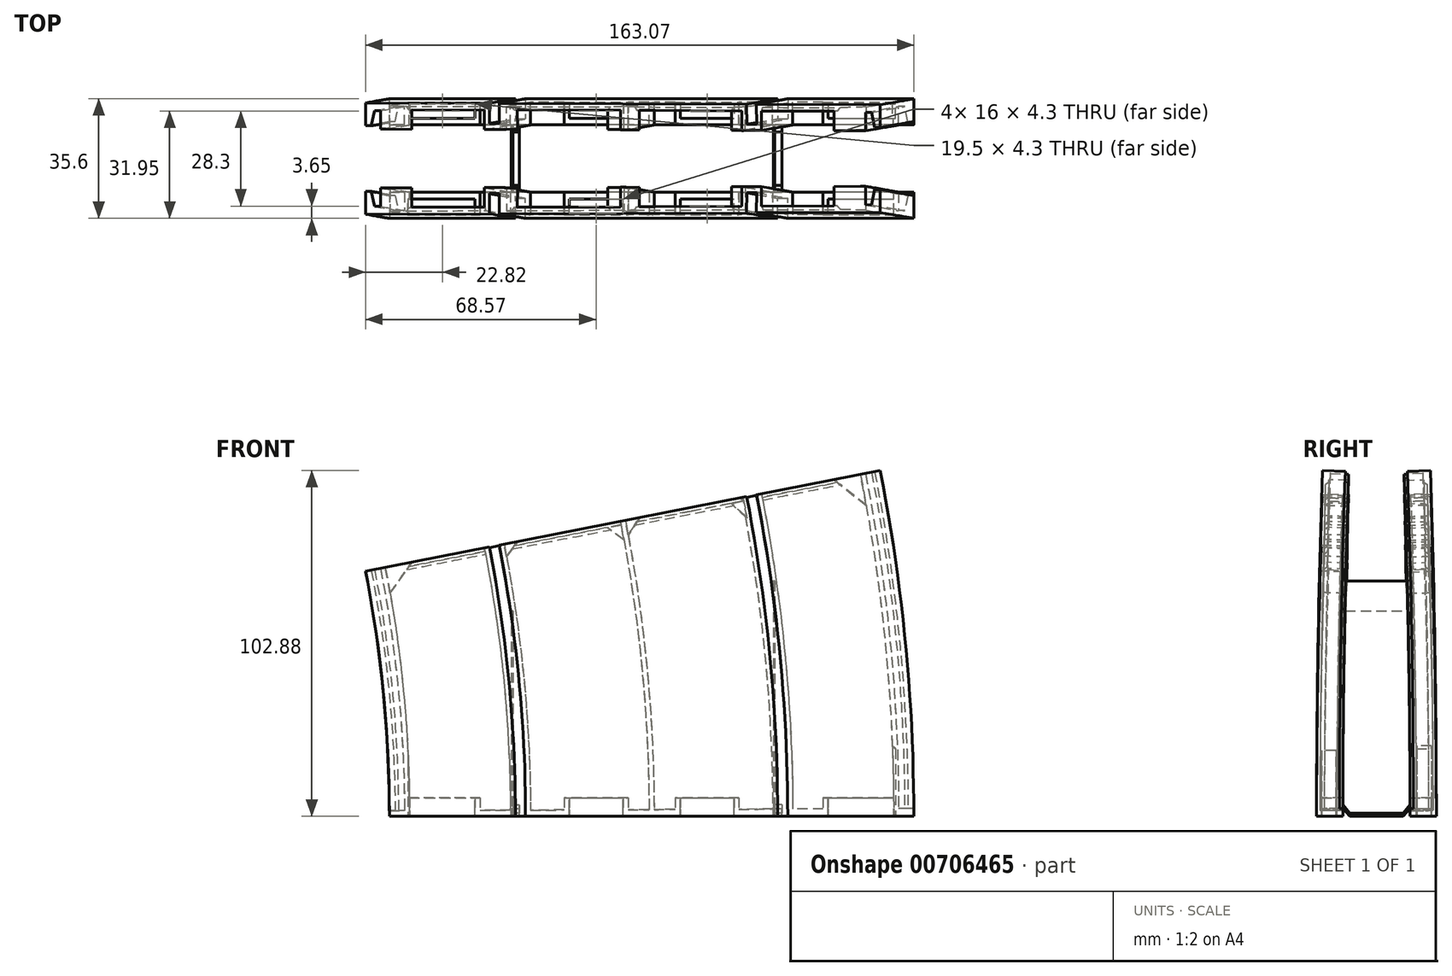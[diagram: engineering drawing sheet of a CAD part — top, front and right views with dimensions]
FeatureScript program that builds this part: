
annotation { "Feature Type Name" : "Feature", "Feature Type Description" : "" }
export const myFeature = defineFeature(function(context is Context, id is Id, definition is map)
    precondition{}
    {
        {
            var Q0;
            Q0=qCreatedBy(makeId("Top.planeOp"),FACE);
            var sketch = newSketch(context, id + "F0", { "sketchPlane" : qUnion([Q0])});
            skLineSegment(sketch, "E0", {"start": v(0, 7.8) * mm, "end": v(37.5, 7.8) * mm});
            skLineSegment(sketch, "E1", {"start": v(156, 0) * mm, "end": v(0, 0) * mm});
            skLineSegment(sketch, "E2", {"start": v(0, 0) * mm, "end": v(0, 7.8) * mm});
            skLineSegment(sketch, "E3.top", {"start": v(37.5, 1.8) * mm, "end": v(40.5, 1.8) * mm});
            skLineSegment(sketch, "E3.left", {"start": v(37.5, 7.8) * mm, "end": v(37.5, 1.8) * mm});
            skLineSegment(sketch, "E3.right", {"start": v(40.5, 7.8) * mm, "end": v(40.5, 1.8) * mm});
            skLineSegment(sketch, "E4.top", {"start": v(115.5, 1.8) * mm, "end": v(118.5, 1.8) * mm});
            skLineSegment(sketch, "E4.left", {"start": v(115.5, 7.8) * mm, "end": v(115.5, 1.8) * mm});
            skLineSegment(sketch, "E4.right", {"start": v(118.5, 7.8) * mm, "end": v(118.5, 1.8) * mm});
            skLineSegment(sketch, "E5.trimOffspring", {"start": v(40.5, 7.8) * mm, "end": v(115.5, 7.8) * mm});
            skLineSegment(sketch, "E6.trimOffspring", {"start": v(118.5, 7.8) * mm, "end": v(156, 7.8) * mm});
            skLineSegment(sketch, "E7.bottom", {"start": v(6, 6.3) * mm, "end": v(25.5, 6.3) * mm});
            skLineSegment(sketch, "E7.top", {"start": v(6, 2) * mm, "end": v(25.5, 2) * mm});
            skLineSegment(sketch, "E7.left", {"start": v(6, 6.3) * mm, "end": v(6, 2) * mm});
            skLineSegment(sketch, "E7.right", {"start": v(25.5, 6.3) * mm, "end": v(25.5, 2) * mm});
            skLineSegment(sketch, "E8.bottom", {"start": v(53.5, 6.3) * mm, "end": v(69.5, 6.3) * mm});
            skLineSegment(sketch, "E8.top", {"start": v(53.5, 2) * mm, "end": v(69.5, 2) * mm});
            skLineSegment(sketch, "E8.left", {"start": v(53.5, 6.3) * mm, "end": v(53.5, 2) * mm});
            skLineSegment(sketch, "E8.right", {"start": v(69.5, 6.3) * mm, "end": v(69.5, 2) * mm});
            skLineSegment(sketch, "E9.bottom", {"start": v(86.5, 6.3) * mm, "end": v(102.5, 6.3) * mm});
            skLineSegment(sketch, "E9.top", {"start": v(86.5, 2) * mm, "end": v(102.5, 2) * mm});
            skLineSegment(sketch, "E9.left", {"start": v(86.5, 6.3) * mm, "end": v(86.5, 2) * mm});
            skLineSegment(sketch, "E9.right", {"start": v(102.5, 6.3) * mm, "end": v(102.5, 2) * mm});
            skLineSegment(sketch, "E10.bottom", {"start": v(130.5, 6.3) * mm, "end": v(150, 6.3) * mm});
            skLineSegment(sketch, "E10.top", {"start": v(130.5, 2) * mm, "end": v(150, 2) * mm});
            skLineSegment(sketch, "E10.left", {"start": v(130.5, 6.3) * mm, "end": v(130.5, 2) * mm});
            skLineSegment(sketch, "E10.right", {"start": v(150, 6.3) * mm, "end": v(150, 2) * mm});
            skLineSegment(sketch, "E11", {"start": v(156, 7.8) * mm, "end": v(156, 0) * mm});
            skLineSegment(sketch, "E12", {"start": v(156, 0) * mm, "end": v(-362, -91.34) * mm});
            skLineSegment(sketch, "E13", {"start": v(-362, -91.34) * mm, "end": v(-356.5, -122.55) * mm});
            skSolve(sketch);
        }
        {
            var Q0;
            Q0=makeQuery(id+"F0.imprint","IMPRINT",FACE,{"disambiguationData":[TD([[makeQuery(id+"F0.imprint","IMPRINT",EDGE,{"derivedFrom":sQuery(id+"F0.wireOp",EDGE,"E0")}),-1.0]])]});
            var Q1;
            Q1=sQuery(id+"F0.wireOp",EDGE,"E13");
            revolve(context, id + "F1", {"surfaceOperationType" : NewSurfaceOperationType.NEW, "entities" : qUnion([Q0]), "axis" : qUnion([Q1]), "revolveType" : RevolveType.ONE_DIRECTION, "angle" : .25 * degree});
        }
        {
            var Q0;
            Q0=makeQuery(id+"F1.opRevolve","CAP_FACE",FACE,{"disambiguationData":[OSD([sQuery(id+"F0.wireOp",EDGE,"E0"),sQuery(id+"F0.wireOp",EDGE,"E1"),sQuery(id+"F0.wireOp",EDGE,"E2"),sQuery(id+"F0.wireOp",EDGE,"E3.top"),sQuery(id+"F0.wireOp",EDGE,"E3.left"),sQuery(id+"F0.wireOp",EDGE,"E3.right"),sQuery(id+"F0.wireOp",EDGE,"E4.top"),sQuery(id+"F0.wireOp",EDGE,"E4.left"),sQuery(id+"F0.wireOp",EDGE,"E4.right"),sQuery(id+"F0.wireOp",EDGE,"E5.trimOffspring"),sQuery(id+"F0.wireOp",EDGE,"E6.trimOffspring"),sQuery(id+"F0.wireOp",EDGE,"E7.bottom"),sQuery(id+"F0.wireOp",EDGE,"E7.top"),sQuery(id+"F0.wireOp",EDGE,"E7.left"),sQuery(id+"F0.wireOp",EDGE,"E7.right"),sQuery(id+"F0.wireOp",EDGE,"E8.bottom"),sQuery(id+"F0.wireOp",EDGE,"E8.top"),sQuery(id+"F0.wireOp",EDGE,"E8.left"),sQuery(id+"F0.wireOp",EDGE,"E8.right"),sQuery(id+"F0.wireOp",EDGE,"E9.bottom"),sQuery(id+"F0.wireOp",EDGE,"E9.top"),sQuery(id+"F0.wireOp",EDGE,"E9.left"),sQuery(id+"F0.wireOp",EDGE,"E9.right"),sQuery(id+"F0.wireOp",EDGE,"E10.bottom"),sQuery(id+"F0.wireOp",EDGE,"E10.top"),sQuery(id+"F0.wireOp",EDGE,"E10.left"),sQuery(id+"F0.wireOp",EDGE,"E10.right"),sQuery(id+"F0.wireOp",EDGE,"E11")])],"isStart":true});
            var sketch = newSketch(context, id + "F2", { "sketchPlane" : qUnion([Q0])});
            skLineSegment(sketch, "E14", {"start": v(156, -1) * mm, "end": v(154.3, -1) * mm});
            skLineSegment(sketch, "E15", {"start": v(154.3, -1) * mm, "end": v(153.3, -5.5) * mm});
            skLineSegment(sketch, "E16", {"start": v(153.3, -5.5) * mm, "end": v(151.5, -5.5) * mm});
            skLineSegment(sketch, "E17", {"start": v(151.5, -5.5) * mm, "end": v(151.5, 0) * mm});
            skLineSegment(sketch, "E18", {"start": v(151.5, 0) * mm, "end": v(150, 0) * mm});
            skLineSegment(sketch, "E19", {"start": v(150, 0) * mm, "end": v(150, -6.8) * mm});
            skLineSegment(sketch, "E20", {"start": v(150, -6.8) * mm, "end": v(120, -6.8) * mm});
            skLineSegment(sketch, "E21", {"start": v(120, -6.8) * mm, "end": v(120, 0) * mm});
            skLineSegment(sketch, "E22", {"start": v(120, 0) * mm, "end": v(114, 0) * mm});
            skLineSegment(sketch, "E23", {"start": v(114, 0) * mm, "end": v(114, -6.8) * mm});
            skLineSegment(sketch, "E24", {"start": v(114, -6.8) * mm, "end": v(78.75, -6.8) * mm});
            skLineSegment(sketch, "E25", {"start": v(42, -6.8) * mm, "end": v(42, 0) * mm});
            skLineSegment(sketch, "E26", {"start": v(42, 0) * mm, "end": v(36, 0) * mm});
            skLineSegment(sketch, "E27", {"start": v(36, 0) * mm, "end": v(36, -6.8) * mm});
            skLineSegment(sketch, "E28", {"start": v(36, -6.8) * mm, "end": v(6, -6.8) * mm});
            skLineSegment(sketch, "E29", {"start": v(6, -6.8) * mm, "end": v(6, 0) * mm});
            skLineSegment(sketch, "E30", {"start": v(6, 0) * mm, "end": v(4.5, 0) * mm});
            skLineSegment(sketch, "E31", {"start": v(4.5, 0) * mm, "end": v(4.5, -5.5) * mm});
            skLineSegment(sketch, "E32", {"start": v(4.5, -5.5) * mm, "end": v(2.7, -5.5) * mm});
            skLineSegment(sketch, "E33", {"start": v(2.7, -5.5) * mm, "end": v(1.7, -1) * mm});
            skLineSegment(sketch, "E34", {"start": v(1.7, -1) * mm, "end": v(0, -1) * mm});
            skLineSegment(sketch, "E35", {"start": v(0, -1) * mm, "end": v(0, -7.8) * mm});
            skLineSegment(sketch, "E36", {"start": v(0, -7.8) * mm, "end": v(156, -7.8) * mm});
            skLineSegment(sketch, "E37", {"start": v(156, -7.8) * mm, "end": v(156, -1) * mm});
            skLineSegment(sketch, "E38", {"start": v(77.25, 0) * mm, "end": v(77.25, -6.8) * mm});
            skLineSegment(sketch, "E39.trimOffspring", {"start": v(77.25, -6.8) * mm, "end": v(42, -6.8) * mm});
            skLineSegment(sketch, "E40", {"start": v(156, 0) * mm, "end": v(-362, 91.34) * mm});
            skLineSegment(sketch, "E41", {"start": v(-362, 91.34) * mm, "end": v(-367.9, 57.9) * mm});
            skLineSegment(sketch, "E42", {"start": v(78.75, 0) * mm, "end": v(78.75, -6.8) * mm});
            skLineSegment(sketch, "E43", {"start": v(77.25, 0) * mm, "end": v(78.75, 0) * mm});
            skSolve(sketch);
        }
        {
            var Q0;
            Q0=makeQuery(id+"F2.imprint","IMPRINT",FACE,{"disambiguationData":[TD([[makeQuery(id+"F2.imprint","IMPRINT",EDGE,{"derivedFrom":sQuery(id+"F2.wireOp",EDGE,"E14")}),1.0]])]});
            var Q1;
            Q1=sQuery(id+"F2.wireOp",EDGE,"E41");
            revolve(context, id + "F3", {"operationType" : NewBodyOperationType.ADD, "surfaceOperationType" : NewSurfaceOperationType.NEW, "entities" : qUnion([Q0]), "axis" : qUnion([Q1]), "revolveType" : RevolveType.ONE_DIRECTION, "oppositeDirection" : true, "angle" : 11.25 * degree});
        }
        {
            var Q0;
            Q0=makeQuery(id+"F1.opRevolve","CAP_FACE",FACE,{"disambiguationData":[OSD([sQuery(id+"F0.wireOp",EDGE,"E0"),sQuery(id+"F0.wireOp",EDGE,"E1"),sQuery(id+"F0.wireOp",EDGE,"E2"),sQuery(id+"F0.wireOp",EDGE,"E3.top"),sQuery(id+"F0.wireOp",EDGE,"E3.left"),sQuery(id+"F0.wireOp",EDGE,"E3.right"),sQuery(id+"F0.wireOp",EDGE,"E4.top"),sQuery(id+"F0.wireOp",EDGE,"E4.left"),sQuery(id+"F0.wireOp",EDGE,"E4.right"),sQuery(id+"F0.wireOp",EDGE,"E5.trimOffspring"),sQuery(id+"F0.wireOp",EDGE,"E6.trimOffspring"),sQuery(id+"F0.wireOp",EDGE,"E7.bottom"),sQuery(id+"F0.wireOp",EDGE,"E7.top"),sQuery(id+"F0.wireOp",EDGE,"E7.left"),sQuery(id+"F0.wireOp",EDGE,"E7.right"),sQuery(id+"F0.wireOp",EDGE,"E8.bottom"),sQuery(id+"F0.wireOp",EDGE,"E8.top"),sQuery(id+"F0.wireOp",EDGE,"E8.left"),sQuery(id+"F0.wireOp",EDGE,"E8.right"),sQuery(id+"F0.wireOp",EDGE,"E9.bottom"),sQuery(id+"F0.wireOp",EDGE,"E9.top"),sQuery(id+"F0.wireOp",EDGE,"E9.left"),sQuery(id+"F0.wireOp",EDGE,"E9.right"),sQuery(id+"F0.wireOp",EDGE,"E10.bottom"),sQuery(id+"F0.wireOp",EDGE,"E10.top"),sQuery(id+"F0.wireOp",EDGE,"E10.left"),sQuery(id+"F0.wireOp",EDGE,"E10.right"),sQuery(id+"F0.wireOp",EDGE,"E11")])],"isStart":true});
            var sketch = newSketch(context, id + "F4", { "sketchPlane" : qUnion([Q0])});
            skLineSegment(sketch, "E44.bottom", {"start": v(6, -2) * mm, "end": v(25.5, -2) * mm});
            skLineSegment(sketch, "E44.top", {"start": v(6, -6.3) * mm, "end": v(25.5, -6.3) * mm});
            skLineSegment(sketch, "E44.left", {"start": v(6, -2) * mm, "end": v(6, -6.3) * mm});
            skLineSegment(sketch, "E44.right", {"start": v(25.5, -2) * mm, "end": v(25.5, -6.3) * mm});
            skLineSegment(sketch, "E45.bottom", {"start": v(53.5, -2) * mm, "end": v(69.5, -2) * mm});
            skLineSegment(sketch, "E45.top", {"start": v(53.5, -6.3) * mm, "end": v(69.5, -6.3) * mm});
            skLineSegment(sketch, "E45.left", {"start": v(53.5, -2) * mm, "end": v(53.5, -6.3) * mm});
            skLineSegment(sketch, "E45.right", {"start": v(69.5, -2) * mm, "end": v(69.5, -6.3) * mm});
            skLineSegment(sketch, "E46.bottom", {"start": v(86.5, -2) * mm, "end": v(102.5, -2) * mm});
            skLineSegment(sketch, "E46.top", {"start": v(86.5, -6.3) * mm, "end": v(102.5, -6.3) * mm});
            skLineSegment(sketch, "E46.left", {"start": v(86.5, -2) * mm, "end": v(86.5, -6.3) * mm});
            skLineSegment(sketch, "E46.right", {"start": v(102.5, -2) * mm, "end": v(102.5, -6.3) * mm});
            skLineSegment(sketch, "E47.bottom", {"start": v(130.5, -2) * mm, "end": v(150, -2) * mm});
            skLineSegment(sketch, "E47.top", {"start": v(130.5, -6.3) * mm, "end": v(150, -6.3) * mm});
            skLineSegment(sketch, "E47.left", {"start": v(130.5, -2) * mm, "end": v(130.5, -6.3) * mm});
            skLineSegment(sketch, "E47.right", {"start": v(150, -2) * mm, "end": v(150, -6.3) * mm});
            skLineSegment(sketch, "E48.bottom", {"start": v(4.5, 0) * mm, "end": v(27, 0) * mm});
            skLineSegment(sketch, "E48.top", {"start": v(4.5, -7.8) * mm, "end": v(27, -7.8) * mm});
            skLineSegment(sketch, "E48.left", {"start": v(4.5, 0) * mm, "end": v(4.5, -7.8) * mm});
            skLineSegment(sketch, "E48.right", {"start": v(27, 0) * mm, "end": v(27, -7.8) * mm});
            skLineSegment(sketch, "E49.bottom", {"start": v(52, 0) * mm, "end": v(71, 0) * mm});
            skLineSegment(sketch, "E49.top", {"start": v(52, -7.8) * mm, "end": v(71, -7.8) * mm});
            skLineSegment(sketch, "E49.left", {"start": v(52, 0) * mm, "end": v(52, -7.8) * mm});
            skLineSegment(sketch, "E49.right", {"start": v(71, 0) * mm, "end": v(71, -7.8) * mm});
            skLineSegment(sketch, "E50.bottom", {"start": v(85, 0) * mm, "end": v(104, 0) * mm});
            skLineSegment(sketch, "E50.top", {"start": v(85, -7.8) * mm, "end": v(104, -7.8) * mm});
            skLineSegment(sketch, "E50.left", {"start": v(85, 0) * mm, "end": v(85, -7.8) * mm});
            skLineSegment(sketch, "E50.right", {"start": v(104, 0) * mm, "end": v(104, -7.8) * mm});
            skLineSegment(sketch, "E51.bottom", {"start": v(129, 0) * mm, "end": v(151.4, 0) * mm});
            skLineSegment(sketch, "E51.top", {"start": v(129, -7.8) * mm, "end": v(151.4, -7.8) * mm});
            skLineSegment(sketch, "E51.left", {"start": v(129, 0) * mm, "end": v(129, -7.8) * mm});
            skLineSegment(sketch, "E51.right", {"start": v(151.4, 0) * mm, "end": v(151.4, -7.8) * mm});
            skSolve(sketch);
        }
        {
            var Q0;
            Q0=makeQuery(id+"F4.imprint","IMPRINT",FACE,{"disambiguationData":[TD([[makeQuery(id+"F4.imprint","IMPRINT",EDGE,{"derivedFrom":sQuery(id+"F4.wireOp",EDGE,"E44.bottom")}),1.0]])]});
            var Q1;
            Q1=makeQuery(id+"F4.imprint","IMPRINT",FACE,{"disambiguationData":[TD([[makeQuery(id+"F4.imprint","IMPRINT",EDGE,{"derivedFrom":sQuery(id+"F4.wireOp",EDGE,"E45.bottom")}),1.0]])]});
            var Q2;
            Q2=makeQuery(id+"F4.imprint","IMPRINT",FACE,{"disambiguationData":[TD([[makeQuery(id+"F4.imprint","IMPRINT",EDGE,{"derivedFrom":sQuery(id+"F4.wireOp",EDGE,"E46.bottom")}),1.0]])]});
            var Q3;
            Q3=makeQuery(id+"F4.imprint","IMPRINT",FACE,{"disambiguationData":[TD([[makeQuery(id+"F4.imprint","IMPRINT",EDGE,{"derivedFrom":sQuery(id+"F4.wireOp",EDGE,"E47.bottom")}),1.0]])]});
            extrude(context, id + "F5", {"entities" : qUnion([Q0, Q1, Q2, Q3]), "operationType" : NewBodyOperationType.ADD, "oppositeDirection" : true, "depth" : 5.5 * mm, "offsetDistance" : 25 * mm});
        }
        {
            var Q0;
            Q0=makeQuery(id+"F3.opRevolve","CAP_FACE",FACE,{"disambiguationData":[OSD([sQuery(id+"F0.wireOp",EDGE,"E3.top"),sQuery(id+"F0.wireOp",EDGE,"E3.left"),sQuery(id+"F0.wireOp",EDGE,"E3.right"),sQuery(id+"F0.wireOp",EDGE,"E4.top"),sQuery(id+"F0.wireOp",EDGE,"E4.left"),sQuery(id+"F0.wireOp",EDGE,"E4.right"),sQuery(id+"F2.wireOp",EDGE,"E14"),sQuery(id+"F2.wireOp",EDGE,"E15"),sQuery(id+"F2.wireOp",EDGE,"E16"),sQuery(id+"F2.wireOp",EDGE,"E17"),sQuery(id+"F2.wireOp",EDGE,"E18"),sQuery(id+"F2.wireOp",EDGE,"E19"),sQuery(id+"F2.wireOp",EDGE,"E20"),sQuery(id+"F2.wireOp",EDGE,"E21"),sQuery(id+"F2.wireOp",EDGE,"E22"),sQuery(id+"F2.wireOp",EDGE,"E23"),sQuery(id+"F2.wireOp",EDGE,"E24"),sQuery(id+"F2.wireOp",EDGE,"E25"),sQuery(id+"F2.wireOp",EDGE,"E26"),sQuery(id+"F2.wireOp",EDGE,"E27"),sQuery(id+"F2.wireOp",EDGE,"E28"),sQuery(id+"F2.wireOp",EDGE,"E29"),sQuery(id+"F2.wireOp",EDGE,"E30"),sQuery(id+"F2.wireOp",EDGE,"E31"),sQuery(id+"F2.wireOp",EDGE,"E32"),sQuery(id+"F2.wireOp",EDGE,"E33"),sQuery(id+"F2.wireOp",EDGE,"E34"),sQuery(id+"F2.wireOp",EDGE,"E35"),sQuery(id+"F2.wireOp",EDGE,"E36"),sQuery(id+"F2.wireOp",EDGE,"E37"),sQuery(id+"F2.wireOp",EDGE,"E38"),sQuery(id+"F2.wireOp",EDGE,"E39.trimOffspring"),sQuery(id+"F2.wireOp",EDGE,"E42"),sQuery(id+"F2.wireOp",EDGE,"E43")])],"isStart":false});
            var sketch = newSketch(context, id + "F6", { "sketchPlane" : qUnion([Q0])});
            skLineSegment(sketch, "E52", {"start": v(12.1, 8.09) * mm, "end": v(43.02, 8.19) * mm});
            skLineSegment(sketch, "E53", {"start": v(43.02, 8.19) * mm, "end": v(43.02, 7.2) * mm});
            skLineSegment(sketch, "E54", {"start": v(43.02, 7.2) * mm, "end": v(12.07, 7.09) * mm});
            skLineSegment(sketch, "E55", {"start": v(12.07, 7.09) * mm, "end": v(12.1, 8.09) * mm});
            skLineSegment(sketch, "E56", {"start": v(84.27, 8.32) * mm, "end": v(84.27, 7.44) * mm});
            skLineSegment(sketch, "E57", {"start": v(84.27, 7.44) * mm, "end": v(48.45, 7.32) * mm});
            skLineSegment(sketch, "E58", {"start": v(48.45, 7.32) * mm, "end": v(48.45, 8.32) * mm});
            skLineSegment(sketch, "E59", {"start": v(48.45, 8.32) * mm, "end": v(84.27, 8.32) * mm});
            skLineSegment(sketch, "E60", {"start": v(121.02, 8.45) * mm, "end": v(121.02, 7.45) * mm});
            skLineSegment(sketch, "E61", {"start": v(121.02, 7.45) * mm, "end": v(85.29, 7.45) * mm});
            skLineSegment(sketch, "E62", {"start": v(85.29, 7.45) * mm, "end": v(85.29, 8.45) * mm});
            skLineSegment(sketch, "E63", {"start": v(85.29, 8.45) * mm, "end": v(121.02, 8.45) * mm});
            skLineSegment(sketch, "E64", {"start": v(163.93, 8.6) * mm, "end": v(163.93, 7.6) * mm});
            skLineSegment(sketch, "E65", {"start": v(163.93, 7.6) * mm, "end": v(126.5, 7.47) * mm});
            skLineSegment(sketch, "E66", {"start": v(126.5, 7.47) * mm, "end": v(126.5, 8.47) * mm});
            skLineSegment(sketch, "E67", {"start": v(126.5, 8.47) * mm, "end": v(163.93, 8.6) * mm});
            skSolve(sketch);
        }
        {
            var Q0;
            {var subQ0=sQuery(id+"F6.wireOp",EDGE,"E53");Q0=makeQuery(id+"F6.imprint","IMPRINT",FACE,{"disambiguationData":[TD([[makeQuery(id+"F6.imprint","IMPRINT",EDGE,{"derivedFrom":subQ0}),1.0]])]});}
            var Q1;
            Q1=makeQuery(id+"F6.imprint","IMPRINT",FACE,{"disambiguationData":[TD([[makeQuery(id+"F6.imprint","IMPRINT",EDGE,{"derivedFrom":sQuery(id+"F6.wireOp",EDGE,"E52")}),-1.0]])]});
            var Q2;
            {var subQ0=sQuery(id+"F6.wireOp",EDGE,"E56");Q2=makeQuery(id+"F6.imprint","IMPRINT",FACE,{"disambiguationData":[TD([[makeQuery(id+"F6.imprint","IMPRINT",EDGE,{"derivedFrom":subQ0}),1.0]])]});}
            var Q3;
            {var subQ1=sQuery(id+"F6.wireOp",EDGE,"E58");Q3=makeQuery(id+"F6.imprint","IMPRINT",FACE,{"disambiguationData":[TD([[makeQuery(id+"F6.imprint","IMPRINT",EDGE,{"derivedFrom":subQ1}),-1.0]])]});}
            var Q4;
            {var subQ0=sQuery(id+"F6.wireOp",EDGE,"E60");Q4=makeQuery(id+"F6.imprint","IMPRINT",FACE,{"disambiguationData":[TD([[makeQuery(id+"F6.imprint","IMPRINT",EDGE,{"derivedFrom":subQ0}),1.0]])]});}
            var Q5;
            {var subQ0=sQuery(id+"F6.wireOp",EDGE,"E62");Q5=makeQuery(id+"F6.imprint","IMPRINT",FACE,{"disambiguationData":[TD([[makeQuery(id+"F6.imprint","IMPRINT",EDGE,{"derivedFrom":subQ0}),-1.0]])]});}
            var Q6;
            {var subQ0=sQuery(id+"F6.wireOp",EDGE,"E65");var subQ1=makeQuery(id+"F3.opRevolve","CAP_EDGE",EDGE,{"disambiguationData":[OSD([sQuery(id+"F2.wireOp",EDGE,"E19")])],"isStart":false});var subQ2=makeQuery(id+"F6.imprint","INTERSECT",VERTEX,{"derivedFrom":[subQ1,subQ0]});Q6=makeQuery(id+"F6.imprint","IMPRINT",FACE,{"disambiguationData":[TD([[makeQuery(id+"F6.imprint","IMPRINT",EDGE,{"disambiguationData":[TD([[subQ2,-1.0]])],"derivedFrom":subQ0}),-1.0]])]});}
            var Q7;
            {var subQ0=sQuery(id+"F6.wireOp",EDGE,"E66");Q7=makeQuery(id+"F6.imprint","IMPRINT",FACE,{"disambiguationData":[TD([[makeQuery(id+"F6.imprint","IMPRINT",EDGE,{"derivedFrom":subQ0}),-1.0]])]});}
            var Q8;
            {var subQ0=sQuery(id+"F6.wireOp",EDGE,"E65");var subQ1=makeQuery(id+"F3.opRevolve","CAP_EDGE",EDGE,{"disambiguationData":[OSD([sQuery(id+"F2.wireOp",EDGE,"E37")])],"isStart":false});var subQ2=makeQuery(id+"F6.imprint","INTERSECT",VERTEX,{"derivedFrom":[subQ1,subQ0]});Q8=makeQuery(id+"F6.imprint","IMPRINT",FACE,{"disambiguationData":[TD([[makeQuery(id+"F6.imprint","IMPRINT",EDGE,{"disambiguationData":[TD([[subQ2,-1.0]])],"derivedFrom":subQ0}),-1.0]])]});}
            var Q9;
            {var subQ0=sQuery(id+"F6.wireOp",EDGE,"E64");Q9=makeQuery(id+"F6.imprint","IMPRINT",FACE,{"disambiguationData":[TD([[makeQuery(id+"F6.imprint","IMPRINT",EDGE,{"derivedFrom":subQ0}),-1.0]])]});}
            extrude(context, id + "F7", {"entities" : qUnion([Q0, Q1, Q2, Q3, Q4, Q5, Q6, Q7, Q8, Q9]), "operationType" : NewBodyOperationType.ADD, "oppositeDirection" : true, "depth" : 1 * mm, "offsetDistance" : 25 * mm});
        }
        {
            var Q0;
            Q0=makeQuery(id+"F7.opExtrude","SWEPT_FACE",FACE,{"disambiguationData":[OSD([sQuery(id+"F6.wireOp",EDGE,"E64")])]});
            var sketch = newSketch(context, id + "F8", { "sketchPlane" : qUnion([Q0])});
            skLineSegment(sketch, "E68", {"start": v(5.61, 71.88) * mm, "end": v(5.64, 71) * mm});
            skLineSegment(sketch, "E69", {"start": v(4.61, 71.84) * mm, "end": v(5.61, 71.88) * mm});
            skLineSegment(sketch, "E70", {"start": v(5.64, 71) * mm, "end": v(4.66, 71.85) * mm});
            skSolve(sketch);
        }
        {
            var Q0;
            Q0=makeQuery(id+"F8.imprint","IMPRINT",FACE,{"disambiguationData":[TD([[makeQuery(id+"F8.imprint","IMPRINT",EDGE,{"derivedFrom":sQuery(id+"F8.wireOp",EDGE,"E68")}),-1.0]])]});
            extrude(context, id + "F9", {"entities" : qUnion([Q0]), "operationType" : NewBodyOperationType.ADD, "oppositeDirection" : true, "depth" : 152 * mm, "offsetDistance" : 25 * mm});
        }
        {
            var Q0;
            Q0=makeQuery(id+"F7.opExtrude","SWEPT_FACE",FACE,{"disambiguationData":[OSD([sQuery(id+"F6.wireOp",EDGE,"E61")])]});
            var sketch = newSketch(context, id + "F10", { "sketchPlane" : qUnion([Q0])});
            skLineSegment(sketch, "E71", {"start": v(74.4, 88.6) * mm, "end": v(70.38, 82.6) * mm});
            skLineSegment(sketch, "E72", {"start": v(70.22, 87.77) * mm, "end": v(74.4, 88.6) * mm});
            skLineSegment(sketch, "E73", {"start": v(70.22, 87.77) * mm, "end": v(69.5, 87.57) * mm});
            skLineSegment(sketch, "E74", {"start": v(69.5, 87.57) * mm, "end": v(70.38, 82.6) * mm});
            skLineSegment(sketch, "E75", {"start": v(100.88, 93.78) * mm, "end": v(105.23, 94.63) * mm});
            skLineSegment(sketch, "E76", {"start": v(105.23, 94.63) * mm, "end": v(106.4, 88.6) * mm});
            skLineSegment(sketch, "E77", {"start": v(106.4, 88.6) * mm, "end": v(100.88, 93.78) * mm});
            skSolve(sketch);
        }
        {
            var Q0;
            {var subQ0=sQuery(id+"F10.wireOp",EDGE,"E72");Q0=makeQuery(id+"F10.imprint","IMPRINT",FACE,{"disambiguationData":[TD([[makeQuery(id+"F10.imprint","IMPRINT",EDGE,{"derivedFrom":subQ0}),1.0]])]});}
            var Q1;
            Q1=makeQuery(id+"F10.imprint","IMPRINT",FACE,{"disambiguationData":[TD([[makeQuery(id+"F10.imprint","IMPRINT",EDGE,{"derivedFrom":sQuery(id+"F10.wireOp",EDGE,"E73")}),1.0]])]});
            var Q2;
            {var subQ4=sQuery(id+"F10.wireOp",EDGE,"E76");Q2=makeQuery(id+"F10.imprint","IMPRINT",FACE,{"disambiguationData":[TD([[makeQuery(id+"F10.imprint","IMPRINT",EDGE,{"derivedFrom":subQ4}),-1.0]])]});}
            var Q3;
            {var subQ1=sQuery(id+"F6.wireOp",EDGE,"E61");var subQ2=sQuery(id+"F6.wireOp",EDGE,"E60");var subQ3=makeQuery(id+"F7.opExtrude","SWEPT_EDGE",EDGE,{"disambiguationData":[OSD([sQuery(id+"F2.wireOp",EDGE,"E23"),subQ2,subQ1])]});Q3=makeQuery(id+"F10.imprint","IMPRINT",FACE,{"disambiguationData":[TD([[makeQuery(id+"F10.imprint","IMPRINT",EDGE,{"derivedFrom":subQ3}),1.0]])]});}
            extrude(context, id + "F11", {"entities" : qUnion([Q0, Q1, Q2, Q3]), "operationType" : NewBodyOperationType.ADD, "oppositeDirection" : true, "depth" : 1.3 * mm, "offsetDistance" : 25 * mm});
        }
        {
            var Q0;
            Q0=makeQuery(id+"F10.imprint","IMPRINT",FACE,{"disambiguationData":[TD([[makeQuery(id+"F10.imprint","IMPRINT",EDGE,{"derivedFrom":sQuery(id+"F10.wireOp",EDGE,"E73")}),1.0]])]});
            var Q1;
            {var subQ0=sQuery(id+"F10.wireOp",EDGE,"E72");Q1=makeQuery(id+"F10.imprint","IMPRINT",FACE,{"disambiguationData":[TD([[makeQuery(id+"F10.imprint","IMPRINT",EDGE,{"derivedFrom":subQ0}),1.0]])]});}
            var Q2;
            {var subQ4=sQuery(id+"F10.wireOp",EDGE,"E76");Q2=makeQuery(id+"F10.imprint","IMPRINT",FACE,{"disambiguationData":[TD([[makeQuery(id+"F10.imprint","IMPRINT",EDGE,{"derivedFrom":subQ4}),-1.0]])]});}
            var Q3;
            {var subQ1=sQuery(id+"F6.wireOp",EDGE,"E61");var subQ2=sQuery(id+"F6.wireOp",EDGE,"E60");var subQ3=makeQuery(id+"F7.opExtrude","SWEPT_EDGE",EDGE,{"disambiguationData":[OSD([sQuery(id+"F2.wireOp",EDGE,"E23"),subQ2,subQ1])]});Q3=makeQuery(id+"F10.imprint","IMPRINT",FACE,{"disambiguationData":[TD([[makeQuery(id+"F10.imprint","IMPRINT",EDGE,{"derivedFrom":subQ3}),1.0]])]});}
            extrude(context, id + "F12", {"entities" : qUnion([Q0, Q1, Q2, Q3]), "operationType" : NewBodyOperationType.ADD, "depth" : 5.85 * mm, "offsetDistance" : 25 * mm});
        }
        {
            var Q0;
            Q0=makeQuery(id+"F7.opExtrude","SWEPT_FACE",FACE,{"disambiguationData":[OSD([sQuery(id+"F6.wireOp",EDGE,"E57")])]});
            var sketch = newSketch(context, id + "F13", { "sketchPlane" : qUnion([Q0])});
            skLineSegment(sketch, "E78", {"start": v(63.86, 86.53) * mm, "end": v(68.77, 87.49) * mm});
            skLineSegment(sketch, "E79", {"start": v(68.77, 87.49) * mm, "end": v(70.38, 81.68) * mm});
            skLineSegment(sketch, "E80", {"start": v(70.38, 81.68) * mm, "end": v(63.86, 86.53) * mm});
            skLineSegment(sketch, "E81", {"start": v(38.1, 81.48) * mm, "end": v(33.3, 80.54) * mm});
            skLineSegment(sketch, "E82", {"start": v(33.3, 80.54) * mm, "end": v(34.16, 76.15) * mm});
            skLineSegment(sketch, "E83", {"start": v(34.16, 76.15) * mm, "end": v(38.1, 81.48) * mm});
            skSolve(sketch);
        }
        {
            var Q0;
            {var subQ1=sQuery(id+"F6.wireOp",EDGE,"E57");var subQ2=makeQuery(id+"F7.opExtrude","SWEPT_EDGE",EDGE,{"disambiguationData":[OSD([sQuery(id+"F2.wireOp",EDGE,"E38"),sQuery(id+"F6.wireOp",EDGE,"E56"),subQ1])]});Q0=makeQuery(id+"F13.imprint","IMPRINT",FACE,{"disambiguationData":[TD([[makeQuery(id+"F13.imprint","IMPRINT",EDGE,{"derivedFrom":subQ2}),1.0]])]});}
            var Q1;
            {var subQ3=sQuery(id+"F13.wireOp",EDGE,"E79");Q1=makeQuery(id+"F13.imprint","IMPRINT",FACE,{"disambiguationData":[TD([[makeQuery(id+"F13.imprint","IMPRINT",EDGE,{"derivedFrom":subQ3}),-1.0]])]});}
            var Q2;
            {var subQ1=sQuery(id+"F6.wireOp",EDGE,"E57");var subQ2=makeQuery(id+"F7.boolean.opBoolean","INTERSECT",EDGE,{"derivedFrom":[makeQuery(id+"F3.opRevolve","SWEPT_FACE",FACE,{"disambiguationData":[OSD([sQuery(id+"F2.wireOp",EDGE,"E25")])]}),makeQuery(id+"F7.opExtrude","SWEPT_FACE",FACE,{"disambiguationData":[OSD([subQ1])]})]});Q2=makeQuery(id+"F13.imprint","IMPRINT",FACE,{"disambiguationData":[TD([[makeQuery(id+"F13.imprint","IMPRINT",EDGE,{"derivedFrom":subQ2}),-1.0]])]});}
            var Q3;
            {var subQ1=sQuery(id+"F13.wireOp",EDGE,"E82");Q3=makeQuery(id+"F13.imprint","IMPRINT",FACE,{"disambiguationData":[TD([[makeQuery(id+"F13.imprint","IMPRINT",EDGE,{"derivedFrom":subQ1}),1.0]])]});}
            extrude(context, id + "F14", {"entities" : qUnion([Q0, Q1, Q2, Q3]), "operationType" : NewBodyOperationType.ADD, "oppositeDirection" : true, "depth" : 1.75 * mm, "offsetDistance" : 25 * mm});
        }
        {
            var Q0;
            {var subQ1=sQuery(id+"F6.wireOp",EDGE,"E57");var subQ2=makeQuery(id+"F7.opExtrude","SWEPT_EDGE",EDGE,{"disambiguationData":[OSD([sQuery(id+"F2.wireOp",EDGE,"E38"),sQuery(id+"F6.wireOp",EDGE,"E56"),subQ1])]});Q0=makeQuery(id+"F13.imprint","IMPRINT",FACE,{"disambiguationData":[TD([[makeQuery(id+"F13.imprint","IMPRINT",EDGE,{"derivedFrom":subQ2}),1.0]])]});}
            var Q1;
            {var subQ3=sQuery(id+"F13.wireOp",EDGE,"E79");Q1=makeQuery(id+"F13.imprint","IMPRINT",FACE,{"disambiguationData":[TD([[makeQuery(id+"F13.imprint","IMPRINT",EDGE,{"derivedFrom":subQ3}),-1.0]])]});}
            var Q2;
            {var subQ1=sQuery(id+"F6.wireOp",EDGE,"E57");var subQ2=makeQuery(id+"F7.boolean.opBoolean","INTERSECT",EDGE,{"derivedFrom":[makeQuery(id+"F3.opRevolve","SWEPT_FACE",FACE,{"disambiguationData":[OSD([sQuery(id+"F2.wireOp",EDGE,"E25")])]}),makeQuery(id+"F7.opExtrude","SWEPT_FACE",FACE,{"disambiguationData":[OSD([subQ1])]})]});Q2=makeQuery(id+"F13.imprint","IMPRINT",FACE,{"disambiguationData":[TD([[makeQuery(id+"F13.imprint","IMPRINT",EDGE,{"derivedFrom":subQ2}),-1.0]])]});}
            var Q3;
            {var subQ1=sQuery(id+"F13.wireOp",EDGE,"E82");Q3=makeQuery(id+"F13.imprint","IMPRINT",FACE,{"disambiguationData":[TD([[makeQuery(id+"F13.imprint","IMPRINT",EDGE,{"derivedFrom":subQ1}),1.0]])]});}
            extrude(context, id + "F15", {"entities" : qUnion([Q0, Q1, Q2, Q3]), "operationType" : NewBodyOperationType.ADD, "depth" : 5.8 * mm, "offsetDistance" : 25 * mm});
        }
        {
            var Q0;
            Q0=makeQuery(id+"F7.opExtrude","SWEPT_FACE",FACE,{"disambiguationData":[OSD([sQuery(id+"F6.wireOp",EDGE,"E54")])]});
            var sketch = newSketch(context, id + "F16", { "sketchPlane" : qUnion([Q0])});
            skLineSegment(sketch, "E84", {"start": v(6.7, 75.34) * mm, "end": v(-1.98, 73.64) * mm});
            skLineSegment(sketch, "E85", {"start": v(-1.98, 73.64) * mm, "end": v(-0.38, 65.41) * mm});
            skLineSegment(sketch, "E86", {"start": v(-0.38, 65.41) * mm, "end": v(6.7, 75.34) * mm});
            skSolve(sketch);
        }
        {
            var Q0;
            {var subQ1=sQuery(id+"F16.wireOp",EDGE,"E85");Q0=makeQuery(id+"F16.imprint","IMPRINT",FACE,{"disambiguationData":[TD([[makeQuery(id+"F16.imprint","IMPRINT",EDGE,{"derivedFrom":subQ1}),1.0]])]});}
            var Q1;
            {var subQ1=sQuery(id+"F6.wireOp",EDGE,"E54");var subQ2=makeQuery(id+"F7.boolean.opBoolean","INTERSECT",EDGE,{"derivedFrom":[makeQuery(id+"F3.boolean.opBoolean","MERGE",FACE,{"derivedFrom":[makeQuery(id+"F1.opRevolve","SWEPT_FACE",FACE,{"disambiguationData":[OSD([sQuery(id+"F0.wireOp",EDGE,"E7.left")])]}),makeQuery(id+"F3.opRevolve","SWEPT_FACE",FACE,{"disambiguationData":[OSD([sQuery(id+"F2.wireOp",EDGE,"E29")])]})]}),makeQuery(id+"F7.opExtrude","SWEPT_FACE",FACE,{"disambiguationData":[OSD([subQ1])]})]});Q1=makeQuery(id+"F16.imprint","IMPRINT",FACE,{"disambiguationData":[TD([[makeQuery(id+"F16.imprint","IMPRINT",EDGE,{"derivedFrom":subQ2}),-1.0]])]});}
            extrude(context, id + "F17", {"entities" : qUnion([Q0, Q1]), "operationType" : NewBodyOperationType.ADD, "oppositeDirection" : true, "depth" : 1.47 * mm, "offsetDistance" : 25 * mm});
        }
        {
            var Q0;
            {var subQ1=sQuery(id+"F16.wireOp",EDGE,"E85");Q0=makeQuery(id+"F16.imprint","IMPRINT",FACE,{"disambiguationData":[TD([[makeQuery(id+"F16.imprint","IMPRINT",EDGE,{"derivedFrom":subQ1}),1.0]])]});}
            var Q1;
            {var subQ1=sQuery(id+"F6.wireOp",EDGE,"E54");var subQ2=makeQuery(id+"F7.boolean.opBoolean","INTERSECT",EDGE,{"derivedFrom":[makeQuery(id+"F3.boolean.opBoolean","MERGE",FACE,{"derivedFrom":[makeQuery(id+"F1.opRevolve","SWEPT_FACE",FACE,{"disambiguationData":[OSD([sQuery(id+"F0.wireOp",EDGE,"E7.left")])]}),makeQuery(id+"F3.opRevolve","SWEPT_FACE",FACE,{"disambiguationData":[OSD([sQuery(id+"F2.wireOp",EDGE,"E29")])]})]}),makeQuery(id+"F7.opExtrude","SWEPT_FACE",FACE,{"disambiguationData":[OSD([subQ1])]})]});Q1=makeQuery(id+"F16.imprint","IMPRINT",FACE,{"disambiguationData":[TD([[makeQuery(id+"F16.imprint","IMPRINT",EDGE,{"derivedFrom":subQ2}),-1.0]])]});}
            extrude(context, id + "F18", {"entities" : qUnion([Q0, Q1]), "operationType" : NewBodyOperationType.ADD, "depth" : 5.8 * mm, "offsetDistance" : 25 * mm});
        }
        {
            var Q0;
            {var subQ4=sQuery(id+"F6.wireOp",EDGE,"E65");Q0=makeQuery(id+"F7.boolean.opBoolean","SPLIT",FACE,{"disambiguationData":[TD([makeQuery(id+"F1.opRevolve","SWEPT_FACE",FACE,{"disambiguationData":[OSD([sQuery(id+"F0.wireOp",EDGE,"E10.right")])]})])],"derivedFrom":makeQuery(id+"F7.opExtrude","SWEPT_FACE",FACE,{"disambiguationData":[OSD([subQ4])]})});}
            var sketch = newSketch(context, id + "F19", { "sketchPlane" : qUnion([Q0])});
            skLineSegment(sketch, "E87", {"start": v(132.31, 99.93) * mm, "end": v(141.08, 101.65) * mm});
            skLineSegment(sketch, "E88", {"start": v(141.08, 101.65) * mm, "end": v(142.56, 91.76) * mm});
            skLineSegment(sketch, "E89", {"start": v(142.56, 91.76) * mm, "end": v(132.31, 99.93) * mm});
            skSolve(sketch);
        }
        {
            var Q0;
            {var subQ1=sQuery(id+"F6.wireOp",EDGE,"E65");var subQ2=makeQuery(id+"F7.opExtrude","SWEPT_FACE",FACE,{"disambiguationData":[OSD([subQ1])]});var subQ3=sQuery(id+"F2.wireOp",EDGE,"E19");var subQ4=makeQuery(id+"F3.opRevolve","SWEPT_FACE",FACE,{"disambiguationData":[OSD([subQ3])]});var subQ5=makeQuery(id+"F1.opRevolve","SWEPT_FACE",FACE,{"disambiguationData":[OSD([sQuery(id+"F0.wireOp",EDGE,"E10.right")])]});var subQ6=makeQuery(id+"F7.boolean.opBoolean","INTERSECT",EDGE,{"derivedFrom":[makeQuery(id+"F3.boolean.opBoolean","MERGE",FACE,{"derivedFrom":[subQ5,subQ4]}),subQ2]});Q0=makeQuery(id+"F19.imprint","IMPRINT",FACE,{"disambiguationData":[TD([[makeQuery(id+"F19.imprint","IMPRINT",EDGE,{"derivedFrom":subQ6}),1.0]])]});}
            var Q1;
            {var subQ1=sQuery(id+"F19.wireOp",EDGE,"E88");Q1=makeQuery(id+"F19.imprint","IMPRINT",FACE,{"disambiguationData":[TD([[makeQuery(id+"F19.imprint","IMPRINT",EDGE,{"derivedFrom":subQ1}),-1.0]])]});}
            extrude(context, id + "F20", {"entities" : qUnion([Q0, Q1]), "operationType" : NewBodyOperationType.ADD, "oppositeDirection" : true, "depth" : 1.5 * mm, "offsetDistance" : 25 * mm});
        }
        {
            var Q0;
            {var subQ1=sQuery(id+"F6.wireOp",EDGE,"E65");var subQ2=makeQuery(id+"F7.opExtrude","SWEPT_FACE",FACE,{"disambiguationData":[OSD([subQ1])]});var subQ3=sQuery(id+"F2.wireOp",EDGE,"E19");var subQ4=makeQuery(id+"F3.opRevolve","SWEPT_FACE",FACE,{"disambiguationData":[OSD([subQ3])]});var subQ5=makeQuery(id+"F1.opRevolve","SWEPT_FACE",FACE,{"disambiguationData":[OSD([sQuery(id+"F0.wireOp",EDGE,"E10.right")])]});var subQ6=makeQuery(id+"F7.boolean.opBoolean","INTERSECT",EDGE,{"derivedFrom":[makeQuery(id+"F3.boolean.opBoolean","MERGE",FACE,{"derivedFrom":[subQ5,subQ4]}),subQ2]});Q0=makeQuery(id+"F19.imprint","IMPRINT",FACE,{"disambiguationData":[TD([[makeQuery(id+"F19.imprint","IMPRINT",EDGE,{"derivedFrom":subQ6}),1.0]])]});}
            var Q1;
            {var subQ1=sQuery(id+"F19.wireOp",EDGE,"E88");Q1=makeQuery(id+"F19.imprint","IMPRINT",FACE,{"disambiguationData":[TD([[makeQuery(id+"F19.imprint","IMPRINT",EDGE,{"derivedFrom":subQ1}),-1.0]])]});}
            extrude(context, id + "F21", {"entities" : qUnion([Q0, Q1]), "operationType" : NewBodyOperationType.ADD, "depth" : 5.8 * mm, "offsetDistance" : 25 * mm});
        }
        {
            var Q0;
            Q0=makeQuery(id+"F1.opRevolve","CAP_FACE",FACE,{"disambiguationData":[OSD([sQuery(id+"F0.wireOp",EDGE,"E0"),sQuery(id+"F0.wireOp",EDGE,"E1"),sQuery(id+"F0.wireOp",EDGE,"E2"),sQuery(id+"F0.wireOp",EDGE,"E3.top"),sQuery(id+"F0.wireOp",EDGE,"E3.left"),sQuery(id+"F0.wireOp",EDGE,"E3.right"),sQuery(id+"F0.wireOp",EDGE,"E4.top"),sQuery(id+"F0.wireOp",EDGE,"E4.left"),sQuery(id+"F0.wireOp",EDGE,"E4.right"),sQuery(id+"F0.wireOp",EDGE,"E5.trimOffspring"),sQuery(id+"F0.wireOp",EDGE,"E6.trimOffspring"),sQuery(id+"F0.wireOp",EDGE,"E7.bottom"),sQuery(id+"F0.wireOp",EDGE,"E7.top"),sQuery(id+"F0.wireOp",EDGE,"E7.left"),sQuery(id+"F0.wireOp",EDGE,"E7.right"),sQuery(id+"F0.wireOp",EDGE,"E8.bottom"),sQuery(id+"F0.wireOp",EDGE,"E8.top"),sQuery(id+"F0.wireOp",EDGE,"E8.left"),sQuery(id+"F0.wireOp",EDGE,"E8.right"),sQuery(id+"F0.wireOp",EDGE,"E9.bottom"),sQuery(id+"F0.wireOp",EDGE,"E9.top"),sQuery(id+"F0.wireOp",EDGE,"E9.left"),sQuery(id+"F0.wireOp",EDGE,"E9.right"),sQuery(id+"F0.wireOp",EDGE,"E10.bottom"),sQuery(id+"F0.wireOp",EDGE,"E10.top"),sQuery(id+"F0.wireOp",EDGE,"E10.left"),sQuery(id+"F0.wireOp",EDGE,"E10.right"),sQuery(id+"F0.wireOp",EDGE,"E11")])],"isStart":true});
            var sketch = newSketch(context, id + "F22", { "sketchPlane" : qUnion([Q0])});
            skLineSegment(sketch, "E90.bottom", {"start": v(37.5, -1.8) * mm, "end": v(40.5, -1.8) * mm});
            skLineSegment(sketch, "E90.top", {"start": v(37.5, -7.8) * mm, "end": v(40.5, -7.8) * mm});
            skLineSegment(sketch, "E90.left", {"start": v(37.5, -1.8) * mm, "end": v(37.5, -7.8) * mm});
            skLineSegment(sketch, "E90.right", {"start": v(40.5, -1.8) * mm, "end": v(40.5, -7.8) * mm});
            skLineSegment(sketch, "E91.bottom", {"start": v(115.5, -1.8) * mm, "end": v(118.5, -1.8) * mm});
            skLineSegment(sketch, "E91.top", {"start": v(115.5, -7.8) * mm, "end": v(118.5, -7.8) * mm});
            skLineSegment(sketch, "E91.left", {"start": v(115.5, -1.8) * mm, "end": v(115.5, -7.8) * mm});
            skLineSegment(sketch, "E91.right", {"start": v(118.5, -1.8) * mm, "end": v(118.5, -7.8) * mm});
            skLineSegment(sketch, "E92.bottom", {"start": v(156, 0) * mm, "end": v(164.44, 0) * mm});
            skLineSegment(sketch, "E92.top", {"start": v(156, -9.05) * mm, "end": v(164.44, -9.05) * mm});
            skLineSegment(sketch, "E92.left", {"start": v(156, 0) * mm, "end": v(156, -9.05) * mm});
            skLineSegment(sketch, "E92.right", {"start": v(164.44, 0) * mm, "end": v(164.44, -9.05) * mm});
            skLineSegment(sketch, "E93", {"start": v(156, 0) * mm, "end": v(-362, 91.34) * mm});
            skLineSegment(sketch, "E94", {"start": v(-362, 91.34) * mm, "end": v(-368.28, 55.75) * mm});
            skSolve(sketch);
        }
        {
            var Q0;
            {var subQ3=sQuery(id+"F22.wireOp",EDGE,"E92.bottom");Q0=makeQuery(id+"F22.imprint","IMPRINT",FACE,{"disambiguationData":[TD([[makeQuery(id+"F22.imprint","IMPRINT",EDGE,{"derivedFrom":subQ3}),-1.0]])]});}
            var Q1;
            Q1=makeQuery(id+"F22.imprint","IMPRINT",FACE,{"disambiguationData":[TD([[makeQuery(id+"F22.imprint","IMPRINT",EDGE,{"derivedFrom":sQuery(id+"F22.wireOp",EDGE,"E91.bottom")}),-1.0]])]});
            var Q2;
            Q2=makeQuery(id+"F22.imprint","IMPRINT",FACE,{"disambiguationData":[TD([[makeQuery(id+"F22.imprint","IMPRINT",EDGE,{"derivedFrom":sQuery(id+"F22.wireOp",EDGE,"E90.bottom")}),-1.0]])]});
            var Q3;
            Q3=sQuery(id+"F22.wireOp",EDGE,"E94");
            revolve(context, id + "F23", {"operationType" : NewBodyOperationType.REMOVE, "surfaceOperationType" : NewSurfaceOperationType.NEW, "entities" : qUnion([Q0, Q1, Q2]), "axis" : qUnion([Q3]), "revolveType" : RevolveType.FULL, "oppositeDirection" : true});
        }
        {
            var Q0;
            Q0=qCreatedBy(makeId("Front.planeOp"),FACE);
            var sketch = newSketch(context, id + "F24", { "sketchPlane" : qUnion([Q0])});
            skLineSegment(sketch, "E95.bottom", {"start": v(36.3, 0) * mm, "end": v(36.7, 0) * mm});
            skLineSegment(sketch, "E95.top", {"start": v(36.3, 61.13) * mm, "end": v(36.7, 61.13) * mm});
            skLineSegment(sketch, "E95.left", {"start": v(36.3, 0) * mm, "end": v(36.3, 61.13) * mm});
            skLineSegment(sketch, "E95.right", {"start": v(36.7, 0) * mm, "end": v(36.7, 61.13) * mm});
            skLineSegment(sketch, "E96.bottom", {"start": v(114.26, 0) * mm, "end": v(114.66, 0) * mm});
            skLineSegment(sketch, "E96.top", {"start": v(114.26, 69.96) * mm, "end": v(114.66, 69.96) * mm});
            skLineSegment(sketch, "E96.left", {"start": v(114.26, 0) * mm, "end": v(114.26, 69.96) * mm});
            skLineSegment(sketch, "E96.right", {"start": v(114.66, 0) * mm, "end": v(114.66, 69.96) * mm});
            skSolve(sketch);
        }
        {
            var Q0;
            Q0=makeQuery(id+"F24.imprint","IMPRINT",FACE,{"disambiguationData":[TD([[makeQuery(id+"F24.imprint","IMPRINT",EDGE,{"derivedFrom":sQuery(id+"F24.wireOp",EDGE,"E96.bottom")}),1.0]])]});
            var Q1;
            Q1=makeQuery(id+"F24.imprint","IMPRINT",FACE,{"disambiguationData":[TD([[makeQuery(id+"F24.imprint","IMPRINT",EDGE,{"derivedFrom":sQuery(id+"F24.wireOp",EDGE,"E95.bottom")}),1.0]])]});
            extrude(context, id + "F25", {"entities" : qUnion([Q0, Q1]), "operationType" : NewBodyOperationType.ADD, "depth" : 10 * mm, "offsetDistance" : 25 * mm});
        }
        {
            var Q0;
            Q0=makeQuery(id+"F25.opExtrude","SWEPT_FACE",FACE,{"disambiguationData":[OSD([sQuery(id+"F24.wireOp",EDGE,"E96.right")])]});
            var sketch = newSketch(context, id + "F26", { "sketchPlane" : qUnion([Q0])});
            skLineSegment(sketch, "E97", {"start": v(0, 2.3) * mm, "end": v(-2.07, 0) * mm});
            skLineSegment(sketch, "E98", {"start": v(-2.07, 0) * mm, "end": v(0, 0) * mm});
            skLineSegment(sketch, "E99", {"start": v(0, 0) * mm, "end": v(0, 2.3) * mm});
            skSolve(sketch);
        }
        {
            var Q0;
            Q0=makeQuery(id+"F26.imprint","IMPRINT",FACE,{"disambiguationData":[TD([[makeQuery(id+"F26.imprint","IMPRINT",EDGE,{"derivedFrom":sQuery(id+"F26.wireOp",EDGE,"E97")}),1.0]])]});
            extrude(context, id + "F27", {"entities" : qUnion([Q0]), "operationType" : NewBodyOperationType.REMOVE, "endBound" : BoundingType.THROUGH_ALL, "oppositeDirection" : true, "depth" : 25 * mm, "offsetDistance" : 25 * mm});
        }
        {
            var Q0;
            Q0=makeQuery(id+"F25.opExtrude","SWEPT_FACE",FACE,{"disambiguationData":[OSD([sQuery(id+"F24.wireOp",EDGE,"E96.right")])]});
            var sketch = newSketch(context, id + "F28", { "sketchPlane" : qUnion([Q0])});
            skLineSegment(sketch, "E100", {"start": v(-10, 0) * mm, "end": v(-2.07, 0) * mm});
            skLineSegment(sketch, "E101", {"start": v(-2.07, 0) * mm, "end": v(0, 2.31) * mm});
            skLineSegment(sketch, "E102", {"start": v(0, 2.31) * mm, "end": v(0, 3.38) * mm});
            skLineSegment(sketch, "E103", {"start": v(0, 3.38) * mm, "end": v(-2.07, 0.95) * mm});
            skLineSegment(sketch, "E104", {"start": v(-2.07, 0.95) * mm, "end": v(-10, 0.95) * mm});
            skLineSegment(sketch, "E105", {"start": v(-10, 0.95) * mm, "end": v(-10, 0) * mm});
            skSolve(sketch);
        }
        {
            var Q0;
            Q0=makeQuery(id+"F28.imprint","IMPRINT",FACE,{"disambiguationData":[TD([[makeQuery(id+"F28.imprint","IMPRINT",EDGE,{"derivedFrom":sQuery(id+"F28.wireOp",EDGE,"E100")}),1.0]])]});
            extrude(context, id + "F29", {"entities" : qUnion([Q0]), "operationType" : NewBodyOperationType.ADD, "depth" : 2.1 * mm, "offsetDistance" : 25 * mm});
        }
        {
            var Q0;
            Q0=makeQuery(id+"F25.opExtrude","SWEPT_FACE",FACE,{"disambiguationData":[OSD([sQuery(id+"F24.wireOp",EDGE,"E95.right")])]});
            var sketch = newSketch(context, id + "F30", { "sketchPlane" : qUnion([Q0])});
            skLineSegment(sketch, "E106", {"start": v(-10, 0) * mm, "end": v(-2.07, 0) * mm});
            skLineSegment(sketch, "E107", {"start": v(-2.07, 0) * mm, "end": v(0, 2.3) * mm});
            skLineSegment(sketch, "E108", {"start": v(0, 2.3) * mm, "end": v(0, 3.36) * mm});
            skLineSegment(sketch, "E109", {"start": v(0, 3.36) * mm, "end": v(-2.07, 0.87) * mm});
            skLineSegment(sketch, "E110", {"start": v(-2.07, 0.87) * mm, "end": v(-10, 0.87) * mm});
            skLineSegment(sketch, "E111", {"start": v(-10, 0.87) * mm, "end": v(-10, 0) * mm});
            skSolve(sketch);
        }
        {
            var Q0;
            Q0=makeQuery(id+"F30.imprint","IMPRINT",FACE,{"disambiguationData":[TD([[makeQuery(id+"F30.imprint","IMPRINT",EDGE,{"derivedFrom":sQuery(id+"F30.wireOp",EDGE,"E106")}),1.0]])]});
            extrude(context, id + "F31", {"entities" : qUnion([Q0]), "operationType" : NewBodyOperationType.ADD, "depth" : 1.97 * mm, "offsetDistance" : 25 * mm});
        }
        {
            var Q0;
            Q0=makeQuery(id+"F1.opRevolve","SWEPT_BODY",BODY,{"disambiguationData":[OSD([sQuery(id+"F0.wireOp",EDGE,"E0"),sQuery(id+"F0.wireOp",EDGE,"E1"),sQuery(id+"F0.wireOp",EDGE,"E2"),sQuery(id+"F0.wireOp",EDGE,"E3.top"),sQuery(id+"F0.wireOp",EDGE,"E3.left"),sQuery(id+"F0.wireOp",EDGE,"E3.right"),sQuery(id+"F0.wireOp",EDGE,"E4.top"),sQuery(id+"F0.wireOp",EDGE,"E4.left"),sQuery(id+"F0.wireOp",EDGE,"E4.right"),sQuery(id+"F0.wireOp",EDGE,"E5.trimOffspring"),sQuery(id+"F0.wireOp",EDGE,"E6.trimOffspring"),sQuery(id+"F0.wireOp",EDGE,"E7.bottom"),sQuery(id+"F0.wireOp",EDGE,"E7.top"),sQuery(id+"F0.wireOp",EDGE,"E7.left"),sQuery(id+"F0.wireOp",EDGE,"E7.right"),sQuery(id+"F0.wireOp",EDGE,"E8.bottom"),sQuery(id+"F0.wireOp",EDGE,"E8.top"),sQuery(id+"F0.wireOp",EDGE,"E8.left"),sQuery(id+"F0.wireOp",EDGE,"E8.right"),sQuery(id+"F0.wireOp",EDGE,"E9.bottom"),sQuery(id+"F0.wireOp",EDGE,"E9.top"),sQuery(id+"F0.wireOp",EDGE,"E9.left"),sQuery(id+"F0.wireOp",EDGE,"E9.right"),sQuery(id+"F0.wireOp",EDGE,"E10.bottom"),sQuery(id+"F0.wireOp",EDGE,"E10.top"),sQuery(id+"F0.wireOp",EDGE,"E10.left"),sQuery(id+"F0.wireOp",EDGE,"E10.right"),sQuery(id+"F0.wireOp",EDGE,"E11")])]});
            var Q1;
            Q1=makeQuery(id+"F29.boolean.opBoolean","MERGE",FACE,{"derivedFrom":[makeQuery(id+"F25.opExtrude","CAP_FACE",FACE,{"disambiguationData":[OSD([sQuery(id+"F24.wireOp",EDGE,"E96.bottom"),sQuery(id+"F24.wireOp",EDGE,"E96.top"),sQuery(id+"F24.wireOp",EDGE,"E96.left"),sQuery(id+"F24.wireOp",EDGE,"E96.right")])],"isStart":false}),makeQuery(id+"F29.opExtrude","SWEPT_FACE",FACE,{"disambiguationData":[OSD([sQuery(id+"F28.wireOp",EDGE,"E105")])]})]});
            mirror(context, id + "F32", {"operationType" : NewBodyOperationType.ADD, "entities" : qUnion([Q0]), "mirrorPlane" : qUnion([Q1])});
        }
        {
            var Q0;
            {var subQ0=sQuery(id+"F0.wireOp",EDGE,"E3.right");var subQ1=sQuery(id+"F0.wireOp",EDGE,"E10.right");var subQ2=sQuery(id+"F0.wireOp",EDGE,"E10.bottom");var subQ3=sQuery(id+"F0.wireOp",EDGE,"E9.right");var subQ4=sQuery(id+"F0.wireOp",EDGE,"E11");var subQ5=sQuery(id+"F0.wireOp",EDGE,"E10.left");var subQ6=sQuery(id+"F0.wireOp",EDGE,"E10.top");var subQ7=sQuery(id+"F0.wireOp",EDGE,"E4.right");var subQ8=sQuery(id+"F0.wireOp",EDGE,"E4.left");var subQ10=sQuery(id+"F0.wireOp",EDGE,"E4.top");var subQ12=sQuery(id+"F0.wireOp",EDGE,"E3.left");var subQ13=sQuery(id+"F0.wireOp",EDGE,"E5.trimOffspring");var subQ14=sQuery(id+"F0.wireOp",EDGE,"E0");var subQ15=sQuery(id+"F0.wireOp",EDGE,"E9.left");var subQ17=sQuery(id+"F0.wireOp",EDGE,"E3.top");var subQ18=sQuery(id+"F0.wireOp",EDGE,"E1");var subQ19=sQuery(id+"F0.wireOp",EDGE,"E2");var subQ20=sQuery(id+"F0.wireOp",EDGE,"E6.trimOffspring");var subQ21=sQuery(id+"F0.wireOp",EDGE,"E7.bottom");var subQ22=sQuery(id+"F0.wireOp",EDGE,"E7.top");var subQ23=sQuery(id+"F0.wireOp",EDGE,"E7.right");var subQ24=sQuery(id+"F0.wireOp",EDGE,"E8.bottom");var subQ25=sQuery(id+"F0.wireOp",EDGE,"E8.top");var subQ26=sQuery(id+"F0.wireOp",EDGE,"E8.left");var subQ27=sQuery(id+"F0.wireOp",EDGE,"E8.right");var subQ28=sQuery(id+"F0.wireOp",EDGE,"E9.bottom");var subQ29=sQuery(id+"F0.wireOp",EDGE,"E9.top");Q0=makeQuery(id+"F27.boolean.opBoolean","SPLIT",FACE,{"disambiguationData":[TD([makeQuery(id+"F1.opRevolve","SWEPT_FACE",FACE,{"disambiguationData":[OSD([subQ14])]})])],"derivedFrom":makeQuery(id+"F25.boolean.opBoolean","MERGE",FACE,{"derivedFrom":[makeQuery(id+"F1.opRevolve","CAP_FACE",FACE,{"disambiguationData":[OSD([subQ14,subQ18,subQ19,subQ17,subQ12,subQ0,subQ10,subQ8,subQ7,subQ13,subQ20,subQ21,subQ22,sQuery(id+"F0.wireOp",EDGE,"E7.left"),subQ23,subQ24,subQ25,subQ26,subQ27,subQ28,subQ29,subQ15,subQ3,subQ2,subQ6,subQ5,subQ1,subQ4])],"isStart":true}),makeQuery(id+"F25.opExtrude","SWEPT_FACE",FACE,{"disambiguationData":[OSD([sQuery(id+"F24.wireOp",EDGE,"E95.bottom")])]}),makeQuery(id+"F25.opExtrude","SWEPT_FACE",FACE,{"disambiguationData":[OSD([sQuery(id+"F24.wireOp",EDGE,"E96.bottom")])]})]})});}
            var sketch = newSketch(context, id + "F33", { "sketchPlane" : qUnion([Q0])});
            skLineSegment(sketch, "E112.bottom", {"start": v(130.5, -2) * mm, "end": v(150.5, -2) * mm});
            skLineSegment(sketch, "E112.top", {"start": v(130.5, -6.3) * mm, "end": v(150.5, -6.3) * mm});
            skLineSegment(sketch, "E112.left", {"start": v(130.5, -2) * mm, "end": v(130.5, -6.3) * mm});
            skLineSegment(sketch, "E112.right", {"start": v(150.5, -2) * mm, "end": v(150.5, -6.3) * mm});
            skSolve(sketch);
        }
        {
            var Q0;
            {var subQ2=sQuery(id+"F33.wireOp",EDGE,"E112.right");Q0=makeQuery(id+"F33.imprint","IMPRINT",FACE,{"disambiguationData":[TD([[makeQuery(id+"F33.imprint","IMPRINT",EDGE,{"derivedFrom":subQ2}),-1.0]])]});}
            var Q1;
            {var subQ0=sQuery(id+"F33.wireOp",EDGE,"E112.left");Q1=makeQuery(id+"F33.imprint","IMPRINT",FACE,{"disambiguationData":[TD([[makeQuery(id+"F33.imprint","IMPRINT",EDGE,{"derivedFrom":subQ0}),-1.0]])]});}
            extrude(context, id + "F34", {"entities" : qUnion([Q0, Q1]), "operationType" : NewBodyOperationType.REMOVE, "oppositeDirection" : true, "depth" : 20 * mm, "offsetDistance" : 25 * mm});
        }
        {
            var Q0;
            Q0=makeQuery(id+"F34.boolean.opBoolean","INTERSECT",EDGE,{"derivedFrom":[makeQuery(id+"F3.boolean.opBoolean","MERGE",FACE,{"derivedFrom":[makeQuery(id+"F1.opRevolve","SWEPT_FACE",FACE,{"disambiguationData":[OSD([sQuery(id+"F0.wireOp",EDGE,"E10.right")])]}),makeQuery(id+"F3.opRevolve","SWEPT_FACE",FACE,{"disambiguationData":[OSD([sQuery(id+"F2.wireOp",EDGE,"E19")])]})]}),makeQuery(id+"F34.opExtrude","CAP_FACE",FACE,{"disambiguationData":[OSD([sQuery(id+"F33.wireOp",EDGE,"E112.bottom"),sQuery(id+"F33.wireOp",EDGE,"E112.top"),sQuery(id+"F33.wireOp",EDGE,"E112.left"),sQuery(id+"F33.wireOp",EDGE,"E112.right")])],"isStart":false})]});
            chamfer(context, id + "F35", {"entities" : qUnion([Q0]), "width" : 1 * mm, "tangentPropagation" : true});
        }
        {
            var Q0;
            {var subQ0=sQuery(id+"F0.wireOp",EDGE,"E3.right");var subQ1=sQuery(id+"F0.wireOp",EDGE,"E10.right");var subQ2=sQuery(id+"F0.wireOp",EDGE,"E10.bottom");var subQ3=sQuery(id+"F0.wireOp",EDGE,"E9.right");var subQ4=sQuery(id+"F0.wireOp",EDGE,"E11");var subQ5=sQuery(id+"F0.wireOp",EDGE,"E10.left");var subQ6=sQuery(id+"F0.wireOp",EDGE,"E10.top");var subQ7=sQuery(id+"F0.wireOp",EDGE,"E4.right");var subQ8=sQuery(id+"F0.wireOp",EDGE,"E4.left");var subQ10=sQuery(id+"F0.wireOp",EDGE,"E4.top");var subQ12=sQuery(id+"F0.wireOp",EDGE,"E3.left");var subQ13=sQuery(id+"F0.wireOp",EDGE,"E5.trimOffspring");var subQ14=sQuery(id+"F0.wireOp",EDGE,"E0");var subQ15=sQuery(id+"F0.wireOp",EDGE,"E9.left");var subQ17=sQuery(id+"F0.wireOp",EDGE,"E3.top");var subQ18=sQuery(id+"F0.wireOp",EDGE,"E1");var subQ19=sQuery(id+"F0.wireOp",EDGE,"E2");var subQ20=sQuery(id+"F0.wireOp",EDGE,"E6.trimOffspring");var subQ21=sQuery(id+"F0.wireOp",EDGE,"E7.bottom");var subQ22=sQuery(id+"F0.wireOp",EDGE,"E7.top");var subQ23=sQuery(id+"F0.wireOp",EDGE,"E7.right");var subQ24=sQuery(id+"F0.wireOp",EDGE,"E8.bottom");var subQ25=sQuery(id+"F0.wireOp",EDGE,"E8.top");var subQ26=sQuery(id+"F0.wireOp",EDGE,"E8.left");var subQ27=sQuery(id+"F0.wireOp",EDGE,"E8.right");var subQ28=sQuery(id+"F0.wireOp",EDGE,"E9.bottom");var subQ29=sQuery(id+"F0.wireOp",EDGE,"E9.top");Q0=makeQuery(id+"F32.opPattern","COPY",FACE,{"derivedFrom":makeQuery(id+"F27.boolean.opBoolean","SPLIT",FACE,{"disambiguationData":[TD([makeQuery(id+"F1.opRevolve","SWEPT_FACE",FACE,{"disambiguationData":[OSD([subQ14])]})])],"derivedFrom":makeQuery(id+"F25.boolean.opBoolean","MERGE",FACE,{"derivedFrom":[makeQuery(id+"F1.opRevolve","CAP_FACE",FACE,{"disambiguationData":[OSD([subQ14,subQ18,subQ19,subQ17,subQ12,subQ0,subQ10,subQ8,subQ7,subQ13,subQ20,subQ21,subQ22,sQuery(id+"F0.wireOp",EDGE,"E7.left"),subQ23,subQ24,subQ25,subQ26,subQ27,subQ28,subQ29,subQ15,subQ3,subQ2,subQ6,subQ5,subQ1,subQ4])],"isStart":true}),makeQuery(id+"F25.opExtrude","SWEPT_FACE",FACE,{"disambiguationData":[OSD([sQuery(id+"F24.wireOp",EDGE,"E95.bottom")])]}),makeQuery(id+"F25.opExtrude","SWEPT_FACE",FACE,{"disambiguationData":[OSD([sQuery(id+"F24.wireOp",EDGE,"E96.bottom")])]})]})}),"instanceName":"1"});}
            var sketch = newSketch(context, id + "F36", { "sketchPlane" : qUnion([Q0])});
            skLineSegment(sketch, "E113.bottom", {"start": v(25.5, 26.3) * mm, "end": v(5.5, 26.3) * mm});
            skLineSegment(sketch, "E113.top", {"start": v(25.5, 22) * mm, "end": v(5.5, 22) * mm});
            skLineSegment(sketch, "E113.left", {"start": v(25.5, 26.3) * mm, "end": v(25.5, 22) * mm});
            skLineSegment(sketch, "E113.right", {"start": v(5.5, 26.3) * mm, "end": v(5.5, 22) * mm});
            skSolve(sketch);
        }
        {
            var Q0;
            {var subQ2=sQuery(id+"F36.wireOp",EDGE,"E113.right");Q0=makeQuery(id+"F36.imprint","IMPRINT",FACE,{"disambiguationData":[TD([[makeQuery(id+"F36.imprint","IMPRINT",EDGE,{"derivedFrom":subQ2}),1.0]])]});}
            var Q1;
            {var subQ0=sQuery(id+"F36.wireOp",EDGE,"E113.left");Q1=makeQuery(id+"F36.imprint","IMPRINT",FACE,{"disambiguationData":[TD([[makeQuery(id+"F36.imprint","IMPRINT",EDGE,{"derivedFrom":subQ0}),-1.0]])]});}
            extrude(context, id + "F37", {"entities" : qUnion([Q0, Q1]), "operationType" : NewBodyOperationType.REMOVE, "oppositeDirection" : true, "depth" : 20 * mm, "offsetDistance" : 25 * mm});
        }
    });
